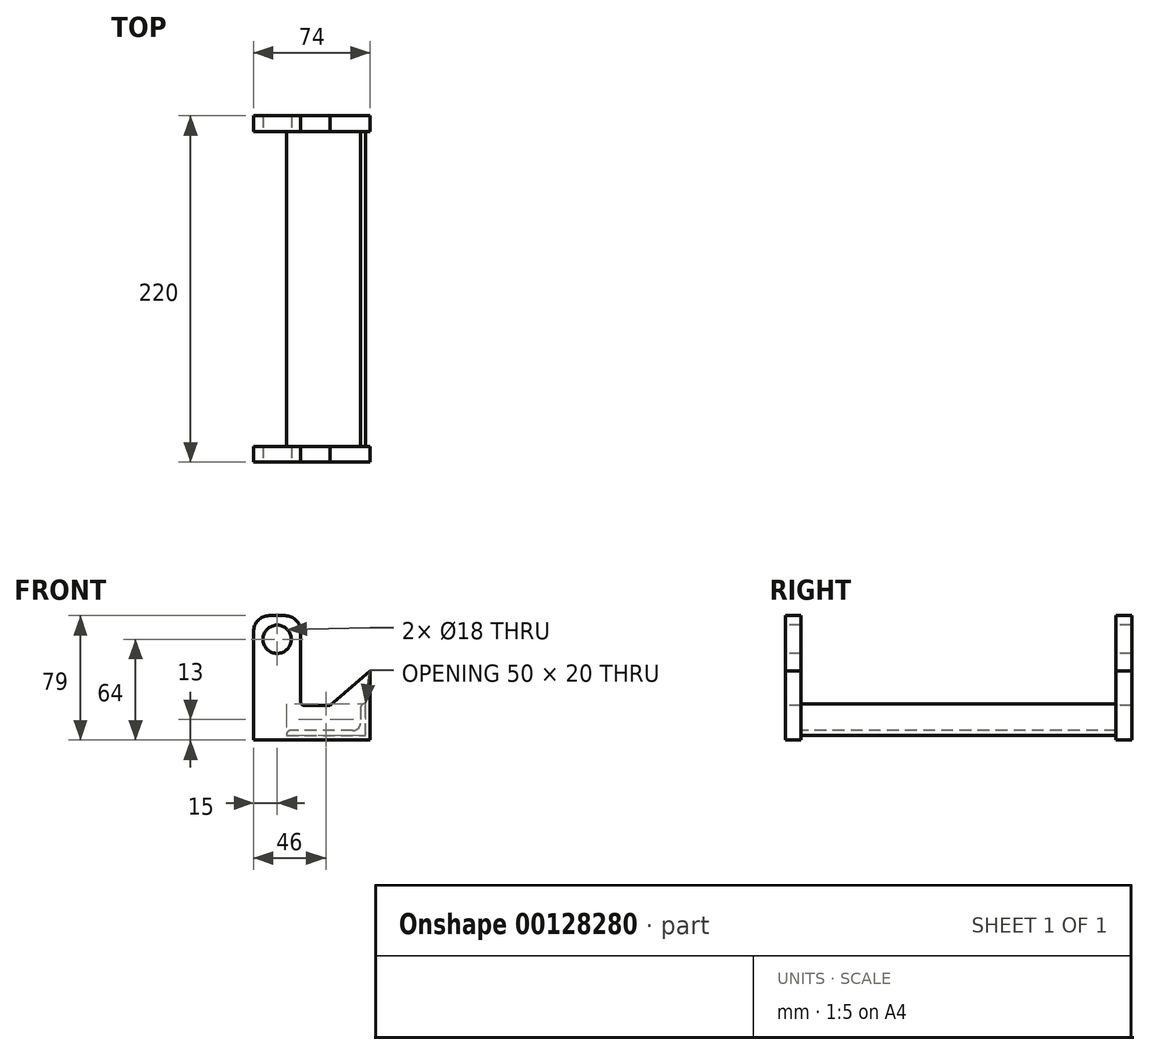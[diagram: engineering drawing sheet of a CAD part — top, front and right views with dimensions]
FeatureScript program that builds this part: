
annotation { "Feature Type Name" : "Feature", "Feature Type Description" : "" }
export const myFeature = defineFeature(function(context is Context, id is Id, definition is map)
    precondition{}
    {
        {
            var Q0;
            Q0=qCreatedBy(makeId("Front.planeOp"),FACE);
            var sketch = newSketch(context, id + "F0", { "sketchPlane" : qUnion([Q0])});
            skLineSegment(sketch, "E0", {"start": v(-15, 5) * mm, "end": v(-15, -64) * mm});
            skLineSegment(sketch, "E1", {"start": v(-15, -64) * mm, "end": v(59, -64) * mm});
            skLineSegment(sketch, "E2", {"start": v(59, -64) * mm, "end": v(59, -20) * mm});
            skLineSegment(sketch, "E3", {"start": v(15, -39.98) * mm, "end": v(15, 5) * mm});
            skLineSegment(sketch, "E4", {"start": v(5, 15) * mm, "end": v(-5, 15) * mm});
            skCircle(sketch, "E5", {"center": v(0, 0) * mm, "radius": 9 * mm});
            skLineSegment(sketch, "E6", {"start": v(17, -41.98) * mm, "end": v(33.45, -41.98) * mm});
            skLineSegment(sketch, "E7", {"start": v(33.45, -41.98) * mm, "end": v(59, -20) * mm});
            skPoint(sketch, "E8.visualSharp", {"position": v(-15, 15) * mm});
            skArc(sketch, "E8.filletArc", {"start": v(-5, 15) * mm, "mid": v(-12.07, 12.07) * mm, "end": v(-15, 5) * mm});
            skPoint(sketch, "E9.visualSharp", {"position": v(15, 15) * mm});
            skArc(sketch, "E9.filletArc", {"start": v(15, 5) * mm, "mid": v(12.07, 12.07) * mm, "end": v(5, 15) * mm});
            skPoint(sketch, "E10.visualSharp", {"position": v(15, -41.98) * mm});
            skArc(sketch, "E10.filletArc", {"start": v(15, -39.98) * mm, "mid": v(15.59, -41.4) * mm, "end": v(17, -41.98) * mm});
            skSolve(sketch);
        }
        {
            var Q0;
            Q0 = qSketchRegion(id + "F0", true);
            extrude(context, id + "F1", {"entities" : qUnion([Q0]), "oppositeDirection" : true, "depth" : 10 * mm});
        }
        {
            var Q0;
            Q0=qCreatedBy(makeId("Front.planeOp"),FACE);
            cPlane(context, id + "F2", {"entities" : qUnion([Q0]), "cplaneType" : CPlaneType.OFFSET, "offset" : 10 * mm, "oppositeDirection" : true, "width" : 150 * mm, "height" : 150 * mm});
        }
        {
            var Q0;
            Q0=qCreatedBy(id+"F2.planeOp",FACE);
            var sketch = newSketch(context, id + "F3", { "sketchPlane" : qUnion([Q0])});
            skLineSegment(sketch, "E11", {"start": v(6, -61) * mm, "end": v(56, -61) * mm});
            skLineSegment(sketch, "E12", {"start": v(56, -61) * mm, "end": v(56, -41) * mm});
            skLineSegment(sketch, "E13", {"start": v(56, -41) * mm, "end": v(55.5, -41) * mm});
            skLineSegment(sketch, "E14", {"start": v(53, -43.5) * mm, "end": v(53, -53) * mm});
            skLineSegment(sketch, "E15", {"start": v(48, -58) * mm, "end": v(8.5, -58) * mm});
            skLineSegment(sketch, "E16", {"start": v(6, -60.5) * mm, "end": v(6, -61) * mm});
            skPoint(sketch, "E17.visualSharp", {"position": v(53, -58) * mm});
            skArc(sketch, "E17.filletArc", {"start": v(48, -58) * mm, "mid": v(51.54, -56.54) * mm, "end": v(53, -53) * mm});
            skPoint(sketch, "E18.visualSharp", {"position": v(6, -58) * mm});
            skArc(sketch, "E18.filletArc", {"start": v(8.5, -58) * mm, "mid": v(6.73, -58.73) * mm, "end": v(6, -60.5) * mm});
            skPoint(sketch, "E19.visualSharp", {"position": v(53, -41) * mm});
            skArc(sketch, "E19.filletArc", {"start": v(55.5, -41) * mm, "mid": v(53.73, -41.73) * mm, "end": v(53, -43.5) * mm});
            skSolve(sketch);
        }
        {
            var Q0;
            Q0 = qSketchRegion(id + "F3", true);
            extrude(context, id + "F4", {"entities" : qUnion([Q0]), "operationType" : NewBodyOperationType.ADD, "oppositeDirection" : true, "depth" : 200 * mm});
        }
        {
            var Q0;
            Q0=qCreatedBy(id+"F2.planeOp",FACE);
            cPlane(context, id + "F5", {"entities" : qUnion([Q0]), "cplaneType" : CPlaneType.OFFSET, "offset" : 200 * mm, "oppositeDirection" : true, "width" : 150 * mm, "height" : 150 * mm});
        }
        {
            var Q0;
            Q0=qCreatedBy(id+"F5.planeOp",FACE);
            var sketch = newSketch(context, id + "F6", { "sketchPlane" : qUnion([Q0])});
            skLineSegment(sketch, "E20", {"start": v(-15, 5) * mm, "end": v(-15, -64) * mm});
            skLineSegment(sketch, "E21", {"start": v(-15, -64) * mm, "end": v(59, -64) * mm});
            skLineSegment(sketch, "E22", {"start": v(59, -64) * mm, "end": v(59, -20) * mm});
            skLineSegment(sketch, "E23", {"start": v(15, -39.98) * mm, "end": v(15, 5) * mm});
            skLineSegment(sketch, "E24", {"start": v(5, 15) * mm, "end": v(-5, 15) * mm});
            skCircle(sketch, "E25", {"center": v(0, 0) * mm, "radius": 9 * mm});
            skLineSegment(sketch, "E26", {"start": v(17, -41.98) * mm, "end": v(33.45, -41.98) * mm});
            skLineSegment(sketch, "E27", {"start": v(33.45, -41.98) * mm, "end": v(59, -20) * mm});
            skPoint(sketch, "E28.visualSharp", {"position": v(-15, 15) * mm});
            skArc(sketch, "E28.filletArc", {"start": v(-5, 15) * mm, "mid": v(-12.07, 12.07) * mm, "end": v(-15, 5) * mm});
            skPoint(sketch, "E29.visualSharp", {"position": v(15, 15) * mm});
            skArc(sketch, "E29.filletArc", {"start": v(15, 5) * mm, "mid": v(12.07, 12.07) * mm, "end": v(5, 15) * mm});
            skPoint(sketch, "E30.visualSharp", {"position": v(15, -41.98) * mm});
            skArc(sketch, "E30.filletArc", {"start": v(15, -39.98) * mm, "mid": v(15.59, -41.4) * mm, "end": v(17, -41.98) * mm});
            skSolve(sketch);
        }
        {
            var Q0;
            Q0 = qSketchRegion(id + "F6", true);
            extrude(context, id + "F7", {"entities" : qUnion([Q0]), "operationType" : NewBodyOperationType.ADD, "oppositeDirection" : true, "depth" : 10 * mm});
        }
    });
